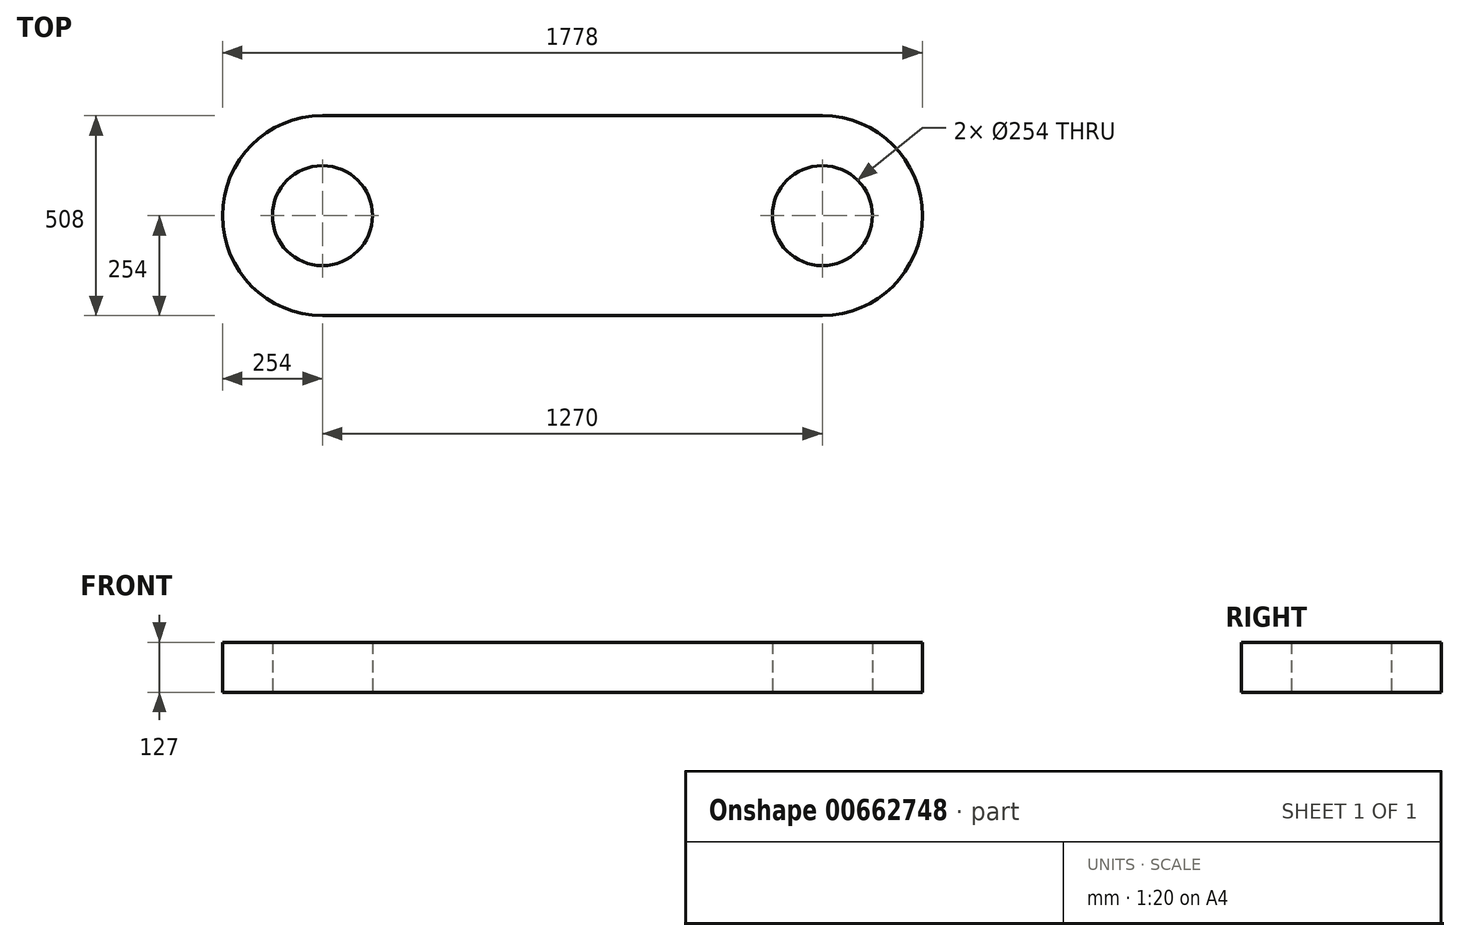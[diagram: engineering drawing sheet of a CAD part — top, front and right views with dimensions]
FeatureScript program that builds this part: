
annotation { "Feature Type Name" : "Feature", "Feature Type Description" : "" }
export const myFeature = defineFeature(function(context is Context, id is Id, definition is map)
    precondition{}
    {
        {
            var Q0;
            Q0=qCreatedBy(makeId("Top.planeOp"),FACE);
            var sketch = newSketch(context, id + "F0", { "sketchPlane" : qUnion([Q0])});
            skLineSegment(sketch, "E0.bottom", {"start": v(-635, 254) * mm, "end": v(635, 254) * mm});
            skLineSegment(sketch, "E0.top", {"start": v(-635, -254) * mm, "end": v(635, -254) * mm});
            skLineSegment(sketch, "E0.left", {"start": v(-635, 254) * mm, "end": v(-635, -254) * mm, "construction": true});
            skLineSegment(sketch, "E0.right", {"start": v(635, 254) * mm, "end": v(635, -254) * mm, "construction": true});
            skArc(sketch, "E1", {"start": v(-635, 254) * mm, "mid": v(-889, 0) * mm, "end": v(-635, -254) * mm});
            skArc(sketch, "E2", {"start": v(635, -254) * mm, "mid": v(889, 0) * mm, "end": v(635, 254) * mm});
            skCircle(sketch, "E3", {"center": v(-635, 0) * mm, "radius": 127 * mm});
            skCircle(sketch, "E4", {"center": v(635, 0) * mm, "radius": 127 * mm});
            skSolve(sketch);
        }
        {
            var Q0;
            Q0 = qSketchRegion(id + "F0", true);
            extrude(context, id + "F1", {"entities" : qUnion([Q0]), "depth" : 127 * mm, "offsetDistance" : 25.4 * mm});
        }
    });
